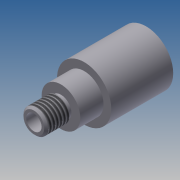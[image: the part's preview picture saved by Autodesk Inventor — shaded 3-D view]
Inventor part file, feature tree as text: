
AUTODESK INVENTOR PART (.ipt)
format: ipt  version: 2012 (Build 160160000, 160)  size: 118,272 bytes
history: native  units: mm
features: thread x2, revolve x1, chamfer x1, sketch x1
ambient origin geometry x8: Origin, YZ Plane, XZ Plane, XY Plane, X Axis, Y Axis, Z Axis, Center Point
bodies: Volumenkörper1 (feature_tree)
feature tree (5):
  revolve  "Umdrehung1"
  chamfer  "Fase1"  Distance=2.7mm
  thread  "Gewinde1"  [1 undecoded]
  thread  "Gewinde2"  [1 undecoded]
  sketch  "Skizze1"  dims[d1=1.0mm d2=2.7mm d3=3.175mm d4=2.0mm d5=4.5mm d6=13.0mm d7=7.0mm d8=5.0mm d9=6.0mm d10=3.0mm d11=7.0mm d12=90.0deg d13=0.5mm d14=2.0mm d15=45.0deg d16=10.0mm d17=0.0mm d18=10.0mm d19=0.0mm]
note: 2 required parameter values undecoded (feature->parameter linkage not recoverable at this tier; creation-order binding heuristic only, values carry confidence <= 0.55)
